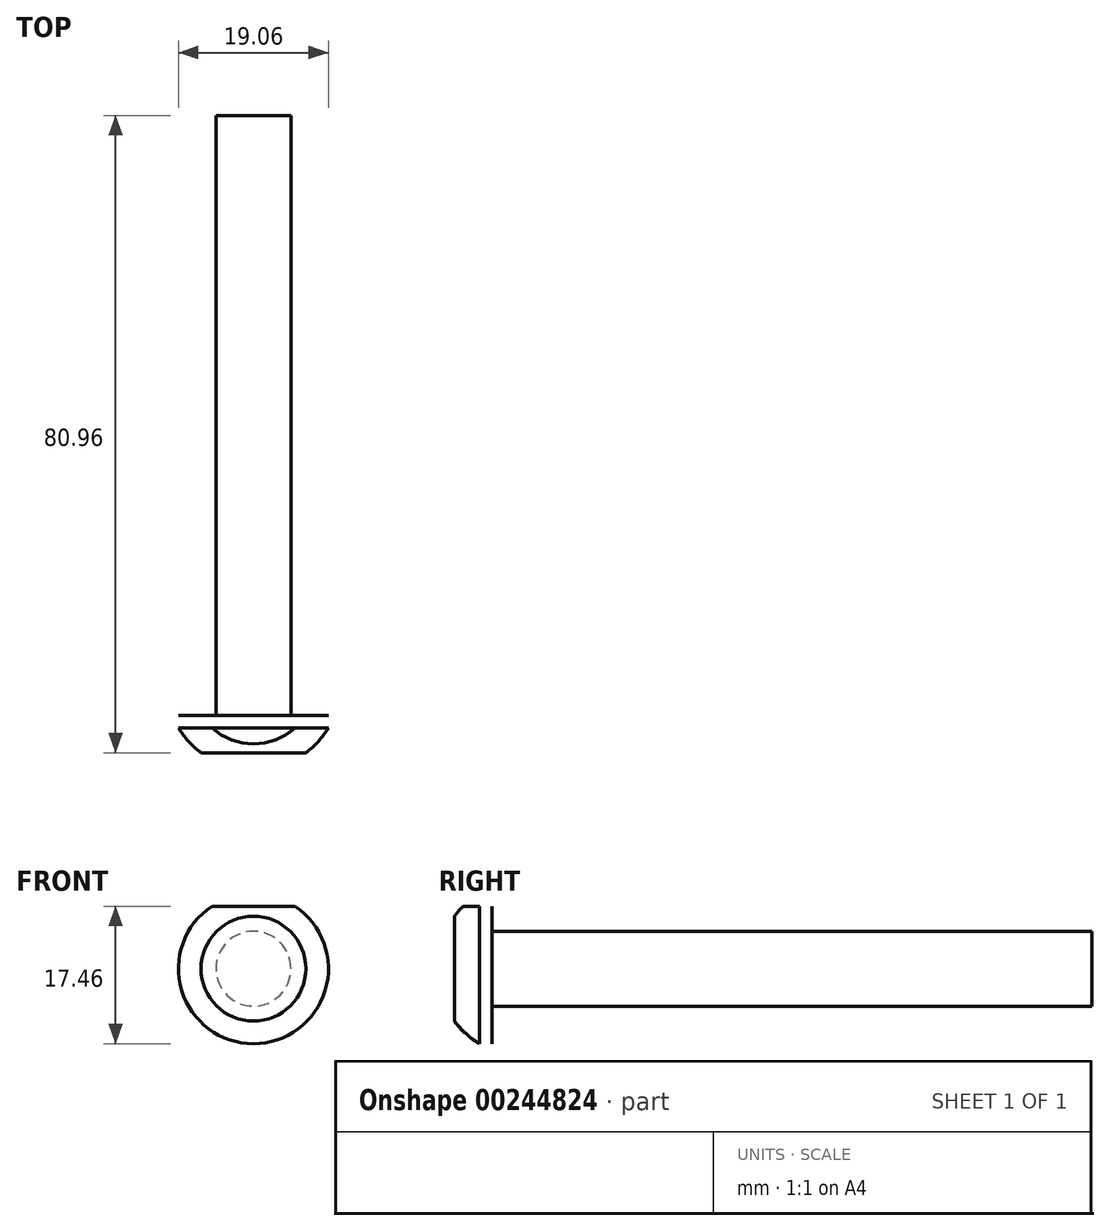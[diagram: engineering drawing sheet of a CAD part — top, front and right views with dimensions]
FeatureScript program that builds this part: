
annotation { "Feature Type Name" : "Feature", "Feature Type Description" : "" }
export const myFeature = defineFeature(function(context is Context, id is Id, definition is map)
    precondition{}
    {
        {
            var Q0;
            Q0=qCreatedBy(makeId("Front.planeOp"),FACE);
            var sketch = newSketch(context, id + "F0", { "sketchPlane" : qUnion([Q0])});
            skCircle(sketch, "E0", {"center": v(0, 5.3) * mm, "radius": 4.76 * mm});
            skSolve(sketch);
        }
        {
            var Q0;
            Q0=makeQuery(id+"F0.imprint","IMPRINT",FACE,{"disambiguationData":[TD([[makeQuery(id+"F0.imprint","IMPRINT",EDGE,{"derivedFrom":sQuery(id+"F0.wireOp",EDGE,"E0")}),1.0]])]});
            extrude(context, id + "F1", {"entities" : qUnion([Q0]), "depth" : 76.2 * mm});
        }
        {
            var Q0;
            Q0=makeQuery(id+"F1.opExtrude","CAP_FACE",FACE,{"disambiguationData":[OSD([sQuery(id+"F0.wireOp",EDGE,"E0")])],"isStart":false});
            var sketch = newSketch(context, id + "F2", { "sketchPlane" : qUnion([Q0])});
            skCircle(sketch, "E1.0.0", {"center": v(0, 5.3) * mm, "radius": 4.76 * mm});
            skCircle(sketch, "E2", {"center": v(0, 5.3) * mm, "radius": 9.53 * mm});
            skSolve(sketch);
        }
        {
            var Q0;
            Q0=makeQuery(id+"F2.imprint","IMPRINT",FACE,{"disambiguationData":[TD([[makeQuery(id+"F2.imprint","IMPRINT",EDGE,{"derivedFrom":sQuery(id+"F2.wireOp",EDGE,"E1.0.0")}),-1.0]])]});
            var Q1;
            Q1=makeQuery(id+"F2.imprint","IMPRINT",FACE,{"disambiguationData":[TD([[makeQuery(id+"F2.imprint","IMPRINT",EDGE,{"derivedFrom":sQuery(id+"F2.wireOp",EDGE,"E1.0.0")}),1.0]])]});
            extrude(context, id + "F3", {"entities" : qUnion([Q0, Q1]), "operationType" : NewBodyOperationType.ADD, "depth" : 1 / 406.4 * mm});
        }
        {
            var Q0;
            Q0=qCreatedBy(makeId("Right.planeOp"),FACE);
            var sketch = newSketch(context, id + "F4", { "sketchPlane" : qUnion([Q0])});
            skLineSegment(sketch, "E3.0.0", {"start": v(-77.79, -4.23) * mm, "end": v(-77.79, 14.82) * mm});
            skLineSegment(sketch, "E4.left", {"start": v(-77.79, 14.82) * mm, "end": v(-77.79, -4.23) * mm});
            skLineSegment(sketch, "E4.right", {"start": v(-80.96, 5.3) * mm, "end": v(-80.96, -1.36) * mm});
            skPoint(sketch, "E5.orphan", {"position": v(-80.96, -4.23) * mm});
            skArc(sketch, "E6.trimOffspring", {"start": v(-80.96, -1.36) * mm, "mid": v(-79.51, -2.95) * mm, "end": v(-77.79, -4.23) * mm});
            skLineSegment(sketch, "E7", {"start": v(-80.96, 5.3) * mm, "end": v(-77.79, 5.3) * mm});
            skPoint(sketch, "E8.end.orphan", {"position": v(-80.96, 11.95) * mm});
            skSolve(sketch);
        }
        {
            var Q0;
            Q0=makeQuery(id+"F4.imprint","IMPRINT",FACE,{"disambiguationData":[TD([[makeQuery(id+"F4.imprint","IMPRINT",EDGE,{"derivedFrom":sQuery(id+"F4.wireOp",EDGE,"E4.right")}),1.0]])]});
            var Q1;
            Q1=sQuery(id+"F4.wireOp",EDGE,"E7");
            revolve(context, id + "F5", {"operationType" : NewBodyOperationType.ADD, "entities" : qUnion([Q0]), "axis" : qUnion([Q1]), "revolveType" : RevolveType.FULL});
        }
        {
            var Q0;
            Q0=makeQuery(id+"F3.opExtrude","CAP_FACE",FACE,{"disambiguationData":[OSD([sQuery(id+"F2.wireOp",EDGE,"E2")])],"isStart":true});
            var sketch = newSketch(context, id + "F6", { "sketchPlane" : qUnion([Q0])});
            skCircle(sketch, "E9.0.0", {"center": v(0, 5.3) * mm, "radius": 9.53 * mm});
            skPoint(sketch, "E10", {"position": v(0, 13.23) * mm});
            skLineSegment(sketch, "E11", {"start": v(0, 13.23) * mm, "end": v(5.27, 13.23) * mm});
            skLineSegment(sketch, "E12", {"start": v(5.27, 13.23) * mm, "end": v(-5.27, 13.23) * mm});
            skSolve(sketch);
        }
        {
            var Q0;
            {var subQ0=sQuery(id+"F6.wireOp",EDGE,"E12");var subQ4=makeQuery(id+"F6.imprint","IMPRINT",VERTEX,{"derivedFrom":subQ0});Q0=makeQuery(id+"F6.imprint","IMPRINT",FACE,{"disambiguationData":[TD([[makeQuery(id+"F6.imprint","IMPRINT",EDGE,{"disambiguationData":[TD([[subQ4,1.0]])],"derivedFrom":subQ0}),-1.0]])]});}
            extrude(context, id + "F7", {"entities" : qUnion([Q0]), "operationType" : NewBodyOperationType.REMOVE, "oppositeDirection" : true, "depth" : 25.4 * mm});
        }
    });
